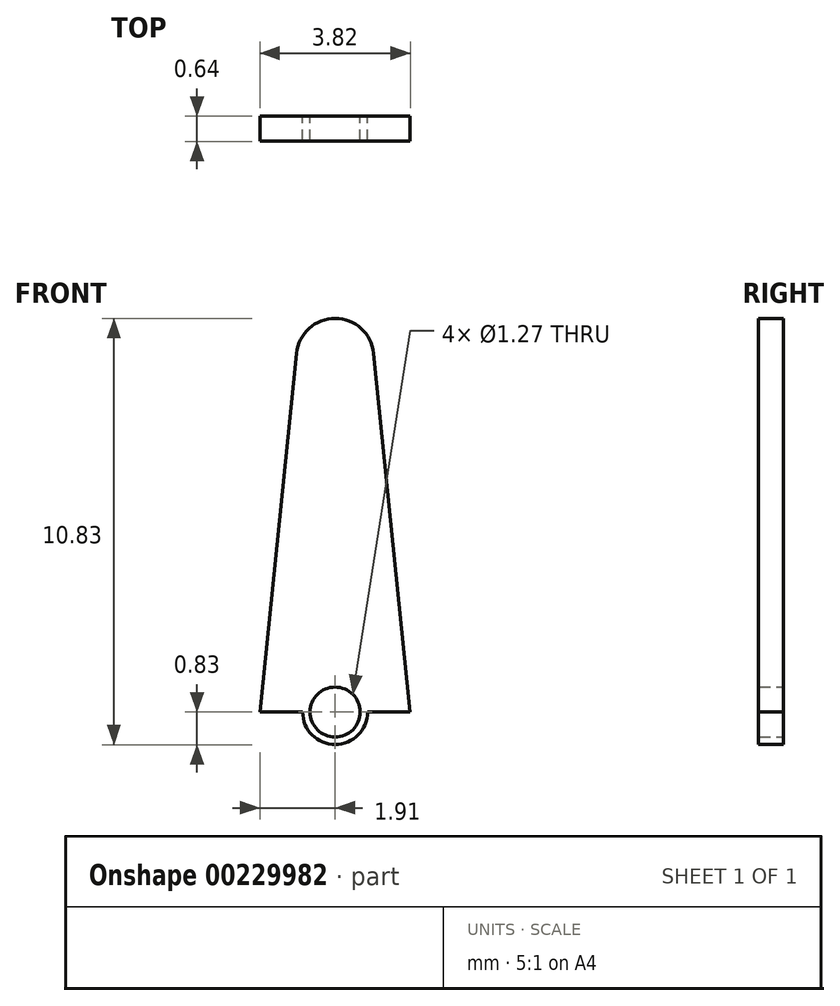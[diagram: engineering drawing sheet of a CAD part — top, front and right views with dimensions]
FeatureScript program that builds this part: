
annotation { "Feature Type Name" : "Feature", "Feature Type Description" : "" }
export const myFeature = defineFeature(function(context is Context, id is Id, definition is map)
    precondition{}
    {
        {
            var Q0;
            Q0=qCreatedBy(makeId("Front.planeOp"),FACE);
            var sketch = newSketch(context, id + "F0", { "sketchPlane" : qUnion([Q0])});
            skLineSegment(sketch, "E0.bottom", {"start": v(-1.9, 0) * mm, "end": v(1.9, 0) * mm});
            skCircle(sketch, "E1", {"center": v(0, 0) * mm, "radius": 0.83 * mm});
            skPoint(sketch, "E2.start.orphan", {"position": v(0, 10) * mm});
            skLineSegment(sketch, "E3", {"start": v(0, 0) * mm, "end": v(0, 10) * mm, "construction": true});
            skLineSegment(sketch, "E4", {"start": v(-1.9, 0) * mm, "end": v(-0.98, 9.12) * mm});
            skLineSegment(sketch, "E5", {"start": v(0, 10) * mm, "end": v(0, 10) * mm});
            skPoint(sketch, "E6.visualSharp", {"position": v(-0.89, 10) * mm});
            skArc(sketch, "E6.filletArc", {"start": v(0, 10) * mm, "mid": v(-0.66, 9.75) * mm, "end": v(-0.98, 9.12) * mm});
            skLineSegment(sketch, "E7.0.MirrorCS", {"start": v(1.9, 0) * mm, "end": v(0.98, 9.12) * mm});
            skArc(sketch, "E8.0.MirrorCS", {"start": v(0, 10) * mm, "mid": v(0.66, 9.75) * mm, "end": v(0.98, 9.12) * mm});
            skSolve(sketch);
        }
        {
            var Q0;
            Q0=qSketchRegion(id+"F0",true);
            extrude(context, id + "F1", {"entities" : qUnion([Q0]), "depth" : 0.64 * mm});
        }
        {
            var Q0;
            {var subQ0=sQuery(id+"F0.wireOp",EDGE,"E1");var subQ1=sQuery(id+"F0.wireOp",EDGE,"E0.bottom");var subQ3=makeQuery(id+"F0.imprint","INTERSECT",VERTEX,{"disambiguationData":[OD(0.0)],"derivedFrom":[subQ1,subQ0]});Q0=makeQuery(id+"F0.imprint","IMPRINT",FACE,{"disambiguationData":[TD([[makeQuery(id+"F0.imprint","IMPRINT",EDGE,{"disambiguationData":[TD([[subQ3,-1.0]])],"derivedFrom":subQ1}),1.0]])]});}
            var sketch = newSketch(context, id + "F2", { "sketchPlane" : qUnion([Q0])});
            skCircle(sketch, "E9", {"center": v(0, 0) * mm, "radius": 0.64 * mm});
            skSolve(sketch);
        }
        {
            var Q0;
            {var subQ0=sQuery(id+"F0.wireOp",EDGE,"E0.bottom");var subQ1=sQuery(id+"F0.wireOp",EDGE,"E1");var subQ2=makeQuery(id+"F0.imprint","IMPRINT",EDGE,{"disambiguationData":[TD([[makeQuery(id+"F0.imprint","INTERSECT",VERTEX,{"disambiguationData":[OD(0.0)],"derivedFrom":[subQ0,subQ1]}),-1.0]])],"derivedFrom":subQ0});var subQ3=sQuery(id+"F2.wireOp",EDGE,"E9");var subQ5=makeQuery(id+"F2.imprint","INTERSECT",VERTEX,{"disambiguationData":[OD(0.0)],"derivedFrom":[subQ2,subQ3]});Q0=makeQuery(id+"F2.imprint","IMPRINT",FACE,{"disambiguationData":[TD([[makeQuery(id+"F2.imprint","IMPRINT",EDGE,{"disambiguationData":[TD([[subQ5,1.0]])],"derivedFrom":subQ3}),1.0]])]});}
            var Q1;
            {var subQ0=sQuery(id+"F0.wireOp",EDGE,"E0.bottom");var subQ1=sQuery(id+"F0.wireOp",EDGE,"E1");var subQ2=makeQuery(id+"F0.imprint","IMPRINT",EDGE,{"disambiguationData":[TD([[makeQuery(id+"F0.imprint","INTERSECT",VERTEX,{"disambiguationData":[OD(0.0)],"derivedFrom":[subQ0,subQ1]}),-1.0]])],"derivedFrom":subQ0});var subQ3=sQuery(id+"F2.wireOp",EDGE,"E9");var subQ5=makeQuery(id+"F2.imprint","INTERSECT",VERTEX,{"disambiguationData":[OD(0.0)],"derivedFrom":[subQ2,subQ3]});Q1=makeQuery(id+"F2.imprint","IMPRINT",FACE,{"disambiguationData":[TD([[makeQuery(id+"F2.imprint","IMPRINT",EDGE,{"disambiguationData":[TD([[subQ5,-1.0]])],"derivedFrom":subQ3}),1.0]])]});}
            extrude(context, id + "F3", {"entities" : qUnion([Q0, Q1]), "operationType" : NewBodyOperationType.REMOVE, "depth" : 25.4 * mm});
        }
    });
